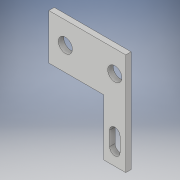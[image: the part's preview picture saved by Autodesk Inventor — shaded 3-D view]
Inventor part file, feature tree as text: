
AUTODESK INVENTOR PART (.ipt)
format: ipt  version: 2017 (Build 210142000, 142)  size: 166,912 bytes
history: native  units: in
note: dims shown in document units (in); Inventor stores cm internally (conversion verified against a paired STEP export)
features: extrude x4, sketch x4
ambient origin geometry x8: Origin, YZ Plane, XZ Plane, XY Plane, X Axis, Y Axis, Z Axis, Center Point
bodies: Solid1 (feature_tree)
feature tree (8):
  extrude  "Extrusion1"  Depth=0.496in
  extrude  "Extrusion2"  Depth=0.615in
  extrude  "Extrusion4"  Depth=0.059in
  extrude  "Extrusion5"  Depth=0.3937in
  sketch  "Sketch1"  dims[d0=0.838in d1=0.496in]
  sketch  "Sketch2"  dims[d2=0.238in d3=0.615in]
  sketch  "Sketch3"  dims[d4=0.059in d5=0.0in d6=0.154in]
  sketch  "Sketch6"  dims[d7=0.238in d8=0.18in d9=0.7874in d11=0.539in d12=0.3937in d14=1.0in d16=1.0in d17=0.0in d18=0.114in d19=0.157in d20=0.119in d24=0.7874in d26=0.156in d27=0.3937in d29=1.0in d31=1.0in d32=0.0in d33=1.0in d34=0.0in]
